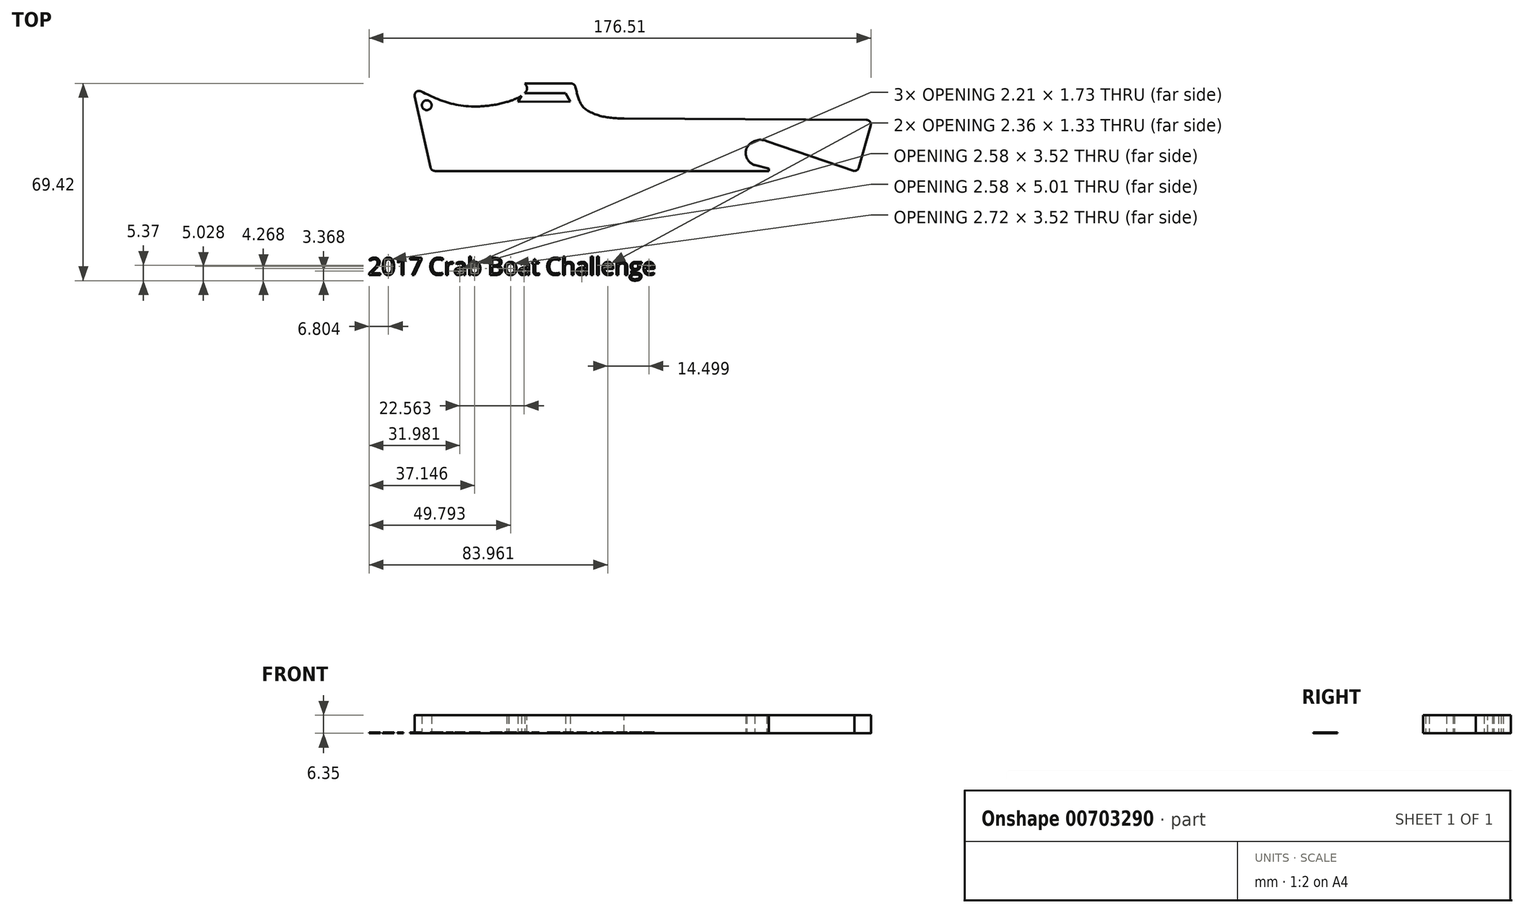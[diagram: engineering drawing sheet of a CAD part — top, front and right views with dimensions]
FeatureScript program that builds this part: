
annotation { "Feature Type Name" : "Feature", "Feature Type Description" : "" }
export const myFeature = defineFeature(function(context is Context, id is Id, definition is map)
    precondition{}
    {
        {
            var Q0;
            Q0=qCreatedBy(makeId("Top.planeOp"),FACE);
            var sketch = newSketch(context, id + "F0", { "sketchPlane" : qUnion([Q0])});
            skLineSegment(sketch, "E0", {"start": v(-84.93, 14.88) * mm, "end": v(-79.38, -10.13) * mm});
            skLineSegment(sketch, "E1", {"start": v(-29.93, 19.42) * mm, "end": v(-53.77, 19.42) * mm});
            skLineSegment(sketch, "E2", {"start": v(-55.2, 17.15) * mm, "end": v(-54.94, 16.58) * mm});
            skLineSegment(sketch, "E3", {"start": v(-54.94, 16.58) * mm, "end": v(-57.7, 12.86) * mm});
            skLineSegment(sketch, "E4", {"start": v(-57.7, 12.86) * mm, "end": v(-62.45, 12.86) * mm});
            skLineSegment(sketch, "E5", {"start": v(-63.96, 11.78) * mm, "end": v(-64.12, 11.3) * mm});
            skLineSegment(sketch, "E6", {"start": v(-46.82, 16.06) * mm, "end": v(-48.57, 12.91) * mm});
            skLineSegment(sketch, "E7", {"start": v(-48.57, 12.91) * mm, "end": v(-30.25, 13.01) * mm});
            skLineSegment(sketch, "E8", {"start": v(-30.25, 13.01) * mm, "end": v(-31.87, 16) * mm});
            skLineSegment(sketch, "E9", {"start": v(-31.87, 16) * mm, "end": v(-46.82, 16.06) * mm});
            skLineSegment(sketch, "E10", {"start": v(-12.87, 7.14) * mm, "end": v(73.94, 6.6) * mm});
            skFitSpline(sketch, "E11", {"points": [v(-28.7, 19.42) * mm, v(-24.4, 10.07) * mm, v(-13.1, 10.5) * mm], "startDerivative": vector(6.33, -23.36) * mm, "endDerivative": vector(13.02, 12.63) * mm});
            skFitSpline(sketch, "E12", {"points": [v(-24.4, 10.07) * mm, v(-12.87, 7.14) * mm, v(9.04, 10.07) * mm], "startDerivative": vector(24.02, -14.85) * mm, "endDerivative": vector(42.16, 10.48) * mm});
            skFitSpline(sketch, "E13", {"points": [v(-85.67, 18.21) * mm, v(-64.12, 11.3) * mm, v(-45.47, 17.35) * mm, v(-67.3, 29.92) * mm], "startDerivative": vector(57.78, -30.56) * mm, "endDerivative": vector(-95.71, 37.44) * mm});
            skLineSegment(sketch, "E14", {"start": v(-51.94, 12.9) * mm, "end": v(-54.94, 12.88) * mm});
            skLineSegment(sketch, "E15", {"start": v(-54.94, 12.88) * mm, "end": v(-52.32, 16.38) * mm});
            skLineSegment(sketch, "E16", {"start": v(-52.32, 16.38) * mm, "end": v(-50.05, 16.29) * mm});
            skLineSegment(sketch, "E17", {"start": v(-50.05, 16.29) * mm, "end": v(-51.94, 12.9) * mm});
            skArc(sketch, "E18.filletArc", {"start": v(-82.66, 16.64) * mm, "mid": v(-84.35, 16.48) * mm, "end": v(-84.93, 14.88) * mm});
            skArc(sketch, "E19.filletArc", {"start": v(-28.39, 18.2) * mm, "mid": v(-28.95, 19.08) * mm, "end": v(-29.93, 19.42) * mm});
            skPoint(sketch, "E20.visualSharp", {"position": v(-79.1, -11.38) * mm});
            skArc(sketch, "E20.filletArc", {"start": v(-79.38, -10.13) * mm, "mid": v(-78.82, -11.03) * mm, "end": v(-77.83, -11.38) * mm});
            skPoint(sketch, "E21.visualSharp", {"position": v(-63.6, 12.86) * mm});
            skArc(sketch, "E21.filletArc", {"start": v(-62.45, 12.86) * mm, "mid": v(-63.38, 12.56) * mm, "end": v(-63.96, 11.78) * mm});
            skPoint(sketch, "E22.visualSharp", {"position": v(-56.29, 19.42) * mm});
            skArc(sketch, "E22.filletArc", {"start": v(-53.77, 19.42) * mm, "mid": v(-55.12, 18.68) * mm, "end": v(-55.2, 17.15) * mm});
            skCircle(sketch, "E23", {"center": v(-80.7, 11.77) * mm, "radius": 1.71 * mm});
            skLineSegment(sketch, "E24", {"start": v(71.25, -10.22) * mm, "end": v(75.46, 4.58) * mm});
            skPoint(sketch, "E25.visualSharp", {"position": v(76.03, 6.58) * mm});
            skArc(sketch, "E25.filletArc", {"start": v(75.46, 4.58) * mm, "mid": v(75.2, 5.96) * mm, "end": v(73.94, 6.6) * mm});
            skPoint(sketch, "E26.visualSharp", {"position": v(70.93, -11.38) * mm});
            skArc(sketch, "E26.filletArc", {"start": v(69.73, -11.38) * mm, "mid": v(70.68, -11.06) * mm, "end": v(71.25, -10.22) * mm});
            skLineSegment(sketch, "E27", {"start": v(38.86, -11.38) * mm, "end": v(-77.83, -11.38) * mm});
            skLineSegment(sketch, "E28", {"start": v(38.86, -11.38) * mm, "end": v(39.61, -11.38) * mm});
            skPoint(sketch, "E29", {"position": v(38.86, -0.85) * mm});
            skPoint(sketch, "E30.orphan", {"position": v(38.86, -8.31) * mm});
            skLineSegment(sketch, "E31", {"start": v(69.73, -11.38) * mm, "end": v(38.86, -0.85) * mm});
            skArc(sketch, "E32", {"start": v(38.86, -0.85) * mm, "mid": v(34.94, -0.73) * mm, "end": v(31.87, -3.18) * mm});
            skArc(sketch, "E33", {"start": v(31.87, -3.18) * mm, "mid": v(31.89, -6.85) * mm, "end": v(34.62, -9.3) * mm});
            skPoint(sketch, "E34.orphan", {"position": v(29.63, -7.6) * mm});
            skPoint(sketch, "E35.start.orphan", {"position": v(38.86, -6.11) * mm});
            skLineSegment(sketch, "E36", {"start": v(39.61, -11.38) * mm, "end": v(39.61, -10.5) * mm});
            skLineSegment(sketch, "E37", {"start": v(39.61, -10.5) * mm, "end": v(34.62, -9.3) * mm});
            skSolve(sketch);
        }
        {
            var Q0;
            Q0=qCreatedBy(makeId("Top.planeOp"),FACE);
            var sketch = newSketch(context, id + "F1", { "sketchPlane" : qUnion([Q0])});
            skText(sketch, "E38", { "text": "2017 Crab Boat Challenge", "fontName": "OpenSans-Regular.ttf"});
            const initialGuessF1  = {"E38": [-0.1014, -0.04798, 1, 0, 0.00606]};
            skSetInitialGuess(sketch, initialGuessF1);
            skSolve(sketch);
        }
        {
            var Q0;
            Q0=makeQuery(id+"F0.imprint","IMPRINT",FACE,{"disambiguationData":[TD([[makeQuery(id+"F0.imprint","IMPRINT",EDGE,{"derivedFrom":sQuery(id+"F0.wireOp",EDGE,"E0")}),1.0]])]});
            extrude(context, id + "F2", {"entities" : qUnion([Q0]), "depth" : 6.35 * mm, "offsetDistance" : 25.4 * mm});
        }
        {
            var Q0;
            Q0 = qSketchRegion(id + "F1", true);
            extrude(context, id + "F3", {"entities" : qUnion([Q0]), "depth" : 0.25 * mm, "offsetDistance" : 25.4 * mm});
        }
    });
